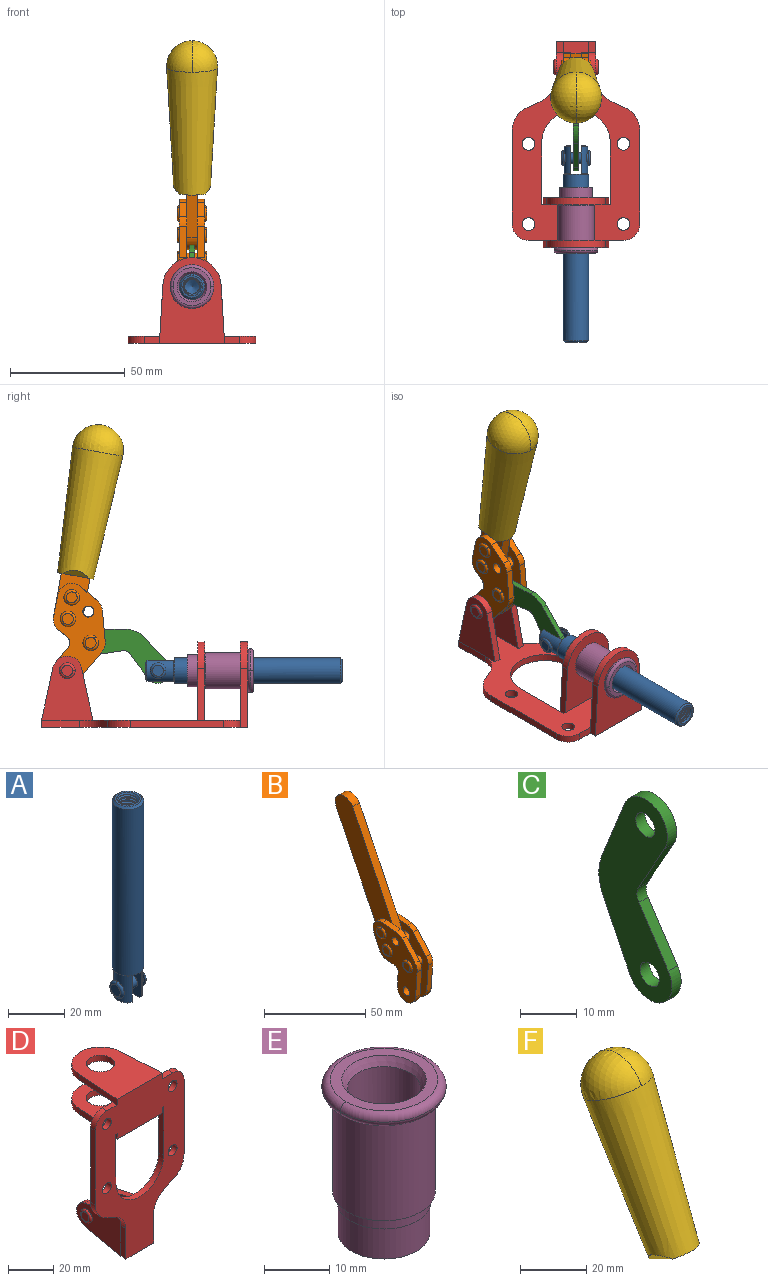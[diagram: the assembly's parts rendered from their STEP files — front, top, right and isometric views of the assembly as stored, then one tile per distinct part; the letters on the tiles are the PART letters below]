
ASSEMBLY  parts=6 mates=6
PART A: 48 faces, bbox 12.6x11.1x86.1 mm
  f0: torus R=2.41mm, axis (-1,0,0), area 15mm2, adj f30,f32,f34
  f1: torus R=2.41mm, axis (-1,0,0), area 15mm2, adj f29,f31,f33
  f2: cylinder r=5.54mm len=72.39mm, axis (0,0,1), area 2518.5mm2, adj f3,f4,f42,f43
  f3: cone r=5.54mm half-angle=45deg, axis (0,0,1), area 7.6mm2, adj f2,f5,f41
  f4: cone r=5.54mm half-angle=45deg, axis (0,0,-1), area 34.9mm2, adj f2,f39
  f5: cylinder r=5.08mm len=11.48mm, axis (0,0,1), area 108.3mm2, adj f3,f7,f8,f41
  f6: cylinder r=2.41mm len=4.83mm, axis (-1,0,0), area 71.2mm2, adj f40,f41
  f7: cylinder r=2.41mm len=4.83mm, axis (-1,0,0), area 7.6mm2, adj f5,f34
  f8: cone r=5.08mm half-angle=45deg, axis (0,0,1), area 10.6mm2, adj f5,f37,f41
  f9: cone r=3.98mm half-angle=45deg, axis (0,0,1), area 17.6mm2, adj f27,f39,f45,f46,f47
  f10: cylinder r=2.41mm len=4.83mm, axis (-1,0,0), area 7.6mm2, adj f33,f38
  f11: cylinder r=3.2mm len=6.4mm, axis (0,0,1), area 78.4mm2, adj f12,f28,f44,f45,f47
  f12: cylinder r=3.2mm len=6.4mm, axis (0,0,1), area 10.5mm2, adj f11,f13,f45,f47
  f13: cylinder r=3.2mm len=6.4mm, axis (0,0,1), area 10.5mm2, adj f12,f14,f45,f47
  f14: cylinder r=3.2mm len=6.4mm, axis (0,0,1), area 10.5mm2, adj f13,f15,f45,f47
  f15: cylinder r=3.2mm len=6.4mm, axis (0,0,1), area 10.5mm2, adj f14,f16,f45,f47
  f16: cylinder r=3.2mm len=6.4mm, axis (0,0,1), area 10.5mm2, adj f15,f17,f45,f47
  f17: cylinder r=3.2mm len=6.4mm, axis (0,0,1), area 10.5mm2, adj f16,f18,f45,f47
  f18: cylinder r=3.2mm len=6.4mm, axis (0,0,1), area 10.5mm2, adj f17,f19,f45,f47
  f19: cylinder r=3.2mm len=6.4mm, axis (0,0,1), area 10.5mm2, adj f18,f20,f45,f47
  f20: cylinder r=3.2mm len=6.4mm, axis (0,0,1), area 10.5mm2, adj f19,f21,f45,f47
  f21: cylinder r=3.2mm len=6.4mm, axis (0,0,1), area 10.5mm2, adj f20,f22,f45,f47
  f22: cylinder r=3.2mm len=6.4mm, axis (0,0,1), area 10.5mm2, adj f21,f23,f45,f47
  f23: cylinder r=3.2mm len=6.4mm, axis (0,0,1), area 10.5mm2, adj f22,f24,f45,f47
  f24: cylinder r=3.2mm len=6.4mm, axis (0,0,1), area 10.5mm2, adj f23,f25,f45,f47
  f25: cylinder r=3.2mm len=6.4mm, axis (0,0,1), area 10.5mm2, adj f24,f26,f45,f47
  f26: cylinder r=3.2mm len=6.4mm, axis (0,0,1), area 10.5mm2, adj f25,f27,f45,f47
  f27: cylinder r=3.2mm len=6.4mm, axis (0,0,1), area 7.4mm2, adj f9,f26,f45,f47
  f28: cone r=3.2mm half-angle=60deg, axis (0,0,1), area 37.2mm2, adj f11
  f29: plane 4.83x4.83mm, normal (-1,0,0), area 18.3mm2, adj f1,f31
  f30: plane 4.83x4.83mm, normal (1,0,0), area 18.3mm2, adj f0,f32
  f31: torus R=2.41mm, axis (-1,0,0), area 15mm2, adj f1,f29,f33
  f32: torus R=2.41mm, axis (-1,0,0), area 15mm2, adj f0,f30,f34
  f33: plane 6.83x6.83mm, normal (1,0,0), area 18.3mm2, adj f1,f10,f31
  f34: plane 6.83x6.83mm, normal (-1,0,0), area 18.3mm2, adj f0,f7,f32
  f35: cone r=5.08mm half-angle=45deg, axis (0,0,1), area 10.6mm2, adj f36,f38,f40
  f36: plane 7.25x1.97mm, normal (0,0,-1), area 10mm2, adj f35,f40
  f37: plane 7.25x1.97mm, normal (0,0,-1), area 10mm2, adj f8,f41
  f38: cylinder r=5.08mm len=11.48mm, axis (0,0,1), area 108.3mm2, adj f10,f35,f40,f42
  f39: plane 9.55x9.55mm, normal (0,0,1), area 22mm2, adj f4,f9
  f40: plane 12.76x10.09mm, normal (1,0,0), area 95.7mm2, adj f6,f35,f36,f38,f42,f43
  f41: plane 12.76x10.09mm, normal (-1,0,0), area 95.7mm2, adj f3,f5,f6,f8,f37,f43
  f42: cone r=5.54mm half-angle=45deg, axis (0,0,1), area 7.6mm2, adj f2,f38,f40
  f43: plane 11.07x4.7mm, normal (0,0,-1), area 50.4mm2, adj f2,f40,f41
  f44: plane 0.89x0.62mm, normal (-1,0,0), area 0.3mm2, adj f11,f45,f46,f47
  f45: bspline ~24.8x7.63mm, area 266.6mm2, adj f9,f11,f12,f13,f14,f15,f16,f17
  f46: bspline ~24.87x7.63mm, area 73.6mm2, adj f9,f44,f45,f47
  f47: bspline ~24.98x7.63mm, area 272.5mm2, adj f9,f11,f12,f13,f14,f15,f16,f17
PART B: 59 faces, bbox 12.9x60.2x99.6 mm
  f0: torus R=2.39mm, axis (-1,0,0), area 14.9mm2, adj f20,f43,f51
  f1: torus R=2.39mm, axis (-1,0,0), area 14.9mm2, adj f19,f42,f51
  f2: torus R=2.39mm, axis (-1,0,0), area 14.9mm2, adj f18,f35,f51
  f3: torus R=2.39mm, axis (-1,0,0), area 14.9mm2, adj f14,f17,f23
  f4: torus R=2.39mm, axis (-1,0,0), area 14.9mm2, adj f13,f16,f23
  f5: torus R=2.39mm, axis (-1,0,0), area 14.9mm2, adj f12,f15,f23
  f6: cylinder r=2.39mm len=4.78mm, axis (1,0,0), area 46.5mm2, adj f48,f50,f51
  f7: cylinder r=2.39mm len=4.78mm, axis (1,0,0), area 46.5mm2, adj f50,f51
  f8: cylinder r=6.35mm len=12.68mm, axis (1,0,0), area 61.8mm2, adj f38,f39,f50,f51
  f9: cylinder r=2.39mm len=4.78mm, axis (-1,0,0), area 70.5mm2, adj f46,f50
  f10: cylinder r=2.39mm len=4.78mm, axis (-1,0,0), area 46.5mm2, adj f23,f45,f46
  f11: cylinder r=2.39mm len=4.78mm, axis (-1,0,0), area 46.5mm2, adj f23,f46
  f12: plane 4.78x4.78mm, normal (1,0,0), area 17.9mm2, adj f5,f15
  f13: plane 4.78x4.78mm, normal (1,0,0), area 17.9mm2, adj f4,f16
  f14: plane 4.78x4.78mm, normal (1,0,0), area 17.9mm2, adj f3,f17
  f15: torus R=2.39mm, axis (-1,0,0), area 14.9mm2, adj f5,f12,f23
  f16: torus R=2.39mm, axis (-1,0,0), area 14.9mm2, adj f4,f13,f23
  f17: torus R=2.39mm, axis (-1,0,0), area 14.9mm2, adj f3,f14,f23
  f18: plane 4.78x4.78mm, normal (-1,0,0), area 17.9mm2, adj f2,f35
  f19: plane 4.78x4.78mm, normal (-1,0,0), area 17.9mm2, adj f1,f42
  f20: plane 4.78x4.78mm, normal (-1,0,0), area 17.9mm2, adj f0,f43
  f21: plane 2.26x0.2mm, normal (1,0,0), area 0.2mm2, adj f31,f44
  f22: plane 2.26x0.2mm, normal (-1,0,0), area 0.2mm2, adj f41,f44
  f23: plane 39.37x30.77mm, normal (1,0,0), area 565.5mm2, adj f3,f4,f5,f10,f11,f15,f16,f17
  f24: cylinder r=6.1mm len=4.15mm, axis (-1,0,0), area 14.7mm2, adj f23,f25,f32,f46
  f25: plane 10.25x9.01mm, normal (0,-0.75,0.66), area 42.3mm2, adj f23,f24,f26,f46
  f26: cylinder r=6.35mm len=4.64mm, axis (-1,0,0), area 15.6mm2, adj f23,f25,f27,f46
  f27: plane 15.84x3.1mm, normal (0,-1,-0.07), area 49.2mm2, adj f23,f26,f28,f46
  f28: cylinder r=6.35mm len=12.68mm, axis (-1,0,0), area 61.8mm2, adj f23,f27,f29,f46
  f29: plane 8.11x3.1mm, normal (0,1,0.07), area 25.2mm2, adj f23,f28,f30,f46
  f30: cylinder r=3.05mm len=3.25mm, axis (-1,0,0), area 14.8mm2, adj f23,f29,f31,f46
  f31: plane 5.99x3.1mm, normal (0,0.07,-1), area 18.6mm2, adj f21,f23,f30,f44,f46
  f32: plane 9.5x3.1mm, normal (0,-0.07,1), area 29.5mm2, adj f23,f24,f33,f46,f47
  f33: cylinder r=6.1mm len=8.63mm, axis (-1,0,0), area 39.1mm2, adj f23,f32,f34,f47
  f34: plane 8.65x3.96mm, normal (0,0.91,-0.42), area 29.5mm2, adj f23,f33,f44,f47
  f35: torus R=2.39mm, axis (-1,0,0), area 14.9mm2, adj f2,f18,f51
  f36: plane 10.25x9.01mm, normal (0,-0.75,0.66), area 42.3mm2, adj f37,f49,f50,f51
  f37: cylinder r=6.35mm len=4.64mm, axis (1,0,0), area 15.6mm2, adj f36,f38,f50,f51
  f38: plane 15.84x3.1mm, normal (0,-1,-0.07), area 49.2mm2, adj f8,f37,f50,f51
  f39: plane 8.11x3.1mm, normal (0,1,0.07), area 25.2mm2, adj f8,f40,f50,f51
  f40: cylinder r=3.05mm len=3.25mm, axis (1,0,0), area 14.8mm2, adj f39,f41,f50,f51
  f41: plane 5.99x3.1mm, normal (0,0.07,-1), area 18.6mm2, adj f22,f40,f44,f50,f51
  f42: torus R=2.39mm, axis (-1,0,0), area 14.9mm2, adj f1,f19,f51
  f43: torus R=2.39mm, axis (-1,0,0), area 14.9mm2, adj f0,f20,f51
  f44: cylinder r=6.35mm len=12.12mm, axis (-1,0,0), area 128.9mm2, adj f21,f22,f23,f31,f34,f41,f46,f47
  f45: plane 2.65x1.35mm, normal (1,0,0), area 1mm2, adj f10,f55
  f46: plane 39.08x20.42mm, normal (-1,0,0), area 412.5mm2, adj f9,f10,f11,f24,f25,f26,f27,f28
  f47: plane 77.62x39.82mm, normal (1,0,0), area 850mm2, adj f32,f33,f34,f44,f53,f54,f55
  f48: plane 2.65x1.35mm, normal (-1,0,0), area 1mm2, adj f6,f55
  f49: cylinder r=6.1mm len=4.15mm, axis (1,0,0), area 14.7mm2, adj f36,f50,f51,f56
  f50: plane 39.08x20.42mm, normal (1,0,0), area 412.5mm2, adj f6,f7,f8,f9,f36,f37,f38,f39
  f51: plane 39.37x30.77mm, normal (-1,0,0), area 565.5mm2, adj f0,f1,f2,f6,f7,f8,f35,f36
  f52: plane 8.65x3.96mm, normal (0,0.91,-0.42), area 29.5mm2, adj f44,f51,f57,f58
  f53: plane 68.49x33.4mm, normal (0,0.9,-0.44), area 358.1mm2, adj f44,f47,f54,f58
  f54: cylinder r=6.35mm len=12.06mm, axis (1,0,0), area 93.7mm2, adj f47,f53,f55,f58
  f55: plane 68.49x33.4mm, normal (0,-0.9,0.44), area 358.1mm2, adj f44,f45,f46,f47,f48,f50,f54,f58
  f56: plane 9.5x3.1mm, normal (0,-0.07,1), area 29.5mm2, adj f49,f50,f51,f57,f58
  f57: cylinder r=6.1mm len=8.63mm, axis (1,0,0), area 39.1mm2, adj f51,f52,f56,f58
  f58: plane 77.62x39.82mm, normal (-1,0,0), area 850mm2, adj f44,f52,f53,f54,f55,f56,f57
PART C: 12 faces, bbox 2.3x18.2x42.8 mm
  f0: cylinder r=2.4mm len=4.8mm, axis (1,0,0), area 34.9mm2, adj f4,f11
  f1: cylinder r=10.41mm len=8.47mm, axis (1,0,0), area 20.2mm2, adj f4,f9,f10,f11
  f2: cylinder r=3.05mm len=3.16mm, axis (1,0,0), area 7.7mm2, adj f4,f6,f7,f11
  f3: cylinder r=2.4mm len=4.8mm, axis (1,0,0), area 34.9mm2, adj f4,f11
  f4: plane 42.81x18.23mm, normal (-1,0,0), area 414.1mm2, adj f0,f1,f2,f3,f5,f6,f7,f8
  f5: cylinder r=5.54mm len=10.67mm, axis (1,0,0), area 41.8mm2, adj f4,f6,f10,f11
  f6: plane 11.66x6.53mm, normal (0,-0.87,-0.49), area 30.9mm2, adj f2,f4,f5,f11
  f7: plane 11.17x7.33mm, normal (0,-0.84,0.55), area 30.9mm2, adj f2,f4,f8,f11
  f8: cylinder r=5.54mm len=10.51mm, axis (1,0,0), area 41.8mm2, adj f4,f7,f9,f11
  f9: plane 13.67x6.67mm, normal (0,0.9,-0.44), area 35.1mm2, adj f1,f4,f8,f11
  f10: plane 14.1x5.7mm, normal (0,0.93,0.37), area 35.1mm2, adj f1,f4,f5,f11
  f11: plane 42.81x18.23mm, normal (1,0,0), area 414.1mm2, adj f0,f1,f2,f3,f5,f6,f7,f8
PART D: 55 faces, bbox 55.7x37.4x89.8 mm
  f0: torus R=2.41mm, axis (-1,0,0), area 15mm2, adj f11,f15,f25
  f1: torus R=2.41mm, axis (-1,0,0), area 15mm2, adj f10,f12,f22
  f2: cylinder r=2.78mm len=5.56mm, axis (0,-1,0), area 54.2mm2, adj f30,f54
  f3: cylinder r=14.99mm len=29.97mm, axis (0,-1,0), area 145.9mm2, adj f30,f49,f53,f54
  f4: cylinder r=2.78mm len=5.56mm, axis (0,-1,0), area 54.2mm2, adj f30,f54
  f5: cylinder r=2.78mm len=5.56mm, axis (0,-1,0), area 54.2mm2, adj f30,f54
  f6: cylinder r=2.78mm len=5.56mm, axis (0,-1,0), area 54.2mm2, adj f30,f54
  f7: cylinder r=6.35mm len=12.7mm, axis (0,0,1), area 123.6mm2, adj f27,f51
  f8: cylinder r=6.35mm len=12.7mm, axis (0,0,-1), area 124.7mm2, adj f21,f35
  f9: cylinder r=2.41mm len=11.18mm, axis (-1,0,0), area 169.4mm2, adj f16,f19
  f10: plane 4.83x4.83mm, normal (1,0,0), area 18.3mm2, adj f1,f12
  f11: plane 4.83x4.83mm, normal (-1,0,0), area 18.3mm2, adj f0,f15
  f12: torus R=2.41mm, axis (-1,0,0), area 15mm2, adj f1,f10,f22
  f13: cylinder r=6.35mm len=12.41mm, axis (1,0,0), area 53.4mm2, adj f18,f19,f22,f23
  f14: cylinder r=6.35mm len=12.41mm, axis (-1,0,0), area 53.4mm2, adj f16,f17,f24,f25
  f15: torus R=2.41mm, axis (-1,0,0), area 15mm2, adj f0,f11,f25
  f16: plane 27.86x22.35mm, normal (1,0,0), area 425.4mm2, adj f9,f14,f17,f24,f30
  f17: plane 22.86x4.97mm, normal (0,0.21,0.98), area 72.5mm2, adj f14,f16,f25,f30
  f18: plane 22.86x4.97mm, normal (0,0.21,0.98), area 72.5mm2, adj f13,f19,f22,f30
  f19: plane 27.86x22.35mm, normal (-1,0,0), area 425.4mm2, adj f9,f13,f18,f23,f30
  f20: cylinder r=12.7mm len=25.35mm, axis (0,0,-1), area 119.8mm2, adj f21,f34,f35,f36
  f21: plane 34.21x28.07mm, normal (0,0,-1), area 702.4mm2, adj f8,f20,f30,f34,f36
  f22: plane 27.96x22.45mm, normal (1,0,0), area 407.2mm2, adj f1,f12,f13,f18,f23,f30,f42,f43
  f23: plane 22.86x4.97mm, normal (0,0.21,-0.98), area 72.5mm2, adj f13,f19,f22,f44
  f24: plane 22.86x4.97mm, normal (0,0.21,-0.98), area 72.5mm2, adj f14,f16,f25,f44
  f25: plane 27.86x22.35mm, normal (-1,0,0), area 407.1mm2, adj f0,f14,f15,f17,f24,f30,f45,f46
  f26: plane 3.1x0.95mm, normal (0,0,-1), area 2.7mm2, adj f30,f49,f50,f54
  f27: plane 34.21x28.07mm, normal (0,0,1), area 702.4mm2, adj f7,f28,f30,f50,f52
  f28: cylinder r=12.7mm len=25.35mm, axis (0,0,1), area 118.8mm2, adj f27,f50,f51,f52
  f29: plane 3.1x0.95mm, normal (0,0,-1), area 2.7mm2, adj f30,f52,f53,f54
  f30: plane 86.54x55.63mm, normal (0,1,0), area 2362.9mm2, adj f2,f3,f4,f5,f6,f16,f17,f18
  f31: plane 40.56x3.1mm, normal (-1,0,0), area 125.7mm2, adj f30,f32,f48,f54
  f32: cylinder r=7.11mm len=7.11mm, axis (0,-1,0), area 34.6mm2, adj f30,f31,f33,f54
  f33: plane 6.67x3.1mm, normal (0,0,1), area 20.4mm2, adj f30,f32,f34,f54
  f34: plane 25.39x3.13mm, normal (-1,0.06,0), area 79.5mm2, adj f20,f21,f33,f35,f54
  f35: plane 37.31x28.45mm, normal (0,0,1), area 789.9mm2, adj f8,f20,f34,f36,f54
  f36: plane 25.39x3.13mm, normal (1,0.06,0), area 79.5mm2, adj f20,f21,f35,f37,f54
  f37: plane 6.67x3.1mm, normal (0,0,1), area 20.4mm2, adj f30,f36,f38,f54
  f38: cylinder r=7.11mm len=7.11mm, axis (0,-1,0), area 34.6mm2, adj f30,f37,f39,f54
  f39: plane 40.56x3.1mm, normal (1,0,0), area 125.7mm2, adj f30,f38,f40,f54
  f40: cylinder r=11.18mm len=10.16mm, axis (0,-1,0), area 39.5mm2, adj f30,f39,f41,f54
  f41: plane 6.09x3.1mm, normal (0.42,0,-0.91), area 20.8mm2, adj f30,f40,f42,f54
  f42: cylinder r=11.18mm len=9.41mm, axis (0,-1,0), area 37.2mm2, adj f22,f30,f41,f43,f54
  f43: plane 16.5x3.1mm, normal (1,0,0), area 51.1mm2, adj f22,f42,f44,f54
  f44: plane 17.37x3.1mm, normal (0,0,-1), area 53.8mm2, adj f23,f24,f30,f43,f45,f54
  f45: plane 16.5x3.1mm, normal (-1,0,0), area 51.1mm2, adj f25,f44,f46,f54
  f46: cylinder r=11.18mm len=9.41mm, axis (0,-1,0), area 37.2mm2, adj f25,f30,f45,f47,f54
  f47: plane 6.09x3.1mm, normal (-0.42,0,-0.91), area 20.8mm2, adj f30,f46,f48,f54
  f48: cylinder r=11.18mm len=10.16mm, axis (0,-1,0), area 39.5mm2, adj f30,f31,f47,f54
  f49: plane 26.54x3.1mm, normal (-1,0,0), area 82.3mm2, adj f3,f26,f30,f54
  f50: plane 25.39x3.1mm, normal (1,0.06,0), area 78.8mm2, adj f26,f27,f28,f51,f54
  f51: plane 37.31x28.45mm, normal (0,0,-1), area 789.9mm2, adj f7,f28,f50,f52,f54
  f52: plane 25.39x3.1mm, normal (-1,0.06,0), area 78.8mm2, adj f27,f28,f29,f51,f54
  f53: plane 26.54x3.1mm, normal (1,0,0), area 82.3mm2, adj f3,f29,f30,f54
  f54: plane 89.66x55.63mm, normal (0,-1,0), area 2678.5mm2, adj f2,f3,f4,f5,f6,f26,f29,f31
PART E: 15 faces, bbox 20.6x20.6x28.7 mm
  f0: torus R=8.26mm, axis (0,0,1), area 56.8mm2, adj f1,f10,f12
  f1: torus R=8.26mm, axis (0,0,1), area 56.8mm2, adj f0,f6,f13
  f2: cylinder r=5.59mm len=25.91mm, axis (0,0,1), area 909.6mm2, adj f3,f4
  f3: cone r=6.86mm half-angle=45deg, axis (0,0,-1), area 70.2mm2, adj f2,f14
  f4: cone r=6.47mm half-angle=30deg, axis (0,0,1), area 66.7mm2, adj f2,f13
  f5: cylinder r=7.04mm len=14.07mm, axis (0,0,1), area 252.6mm2, adj f11,f14
  f6: torus R=8.26mm, axis (0,0,1), area 56.8mm2, adj f1,f12,f13
  f7: cylinder r=7.16mm len=14.33mm, axis (0,0,1), area 91.5mm2, adj f9,f11
  f8: cylinder r=7.86mm len=18.42mm, axis (0,0,1), area 909.6mm2, adj f9,f10
  f9: plane 15.72x15.72mm, normal (0,0,-1), area 33mm2, adj f7,f8
  f10: plane 16.51x16.51mm, normal (0,0,-1), area 19.9mm2, adj f0,f8,f12
  f11: plane 14.33x14.33mm, normal (0,0,-1), area 5.7mm2, adj f5,f7
  f12: torus R=8.26mm, axis (0,0,1), area 56.8mm2, adj f0,f6,f10
  f13: plane 16.51x16.51mm, normal (0,0,1), area 82.7mm2, adj f1,f4,f6
  f14: plane 14.07x14.07mm, normal (0,0,-1), area 7.8mm2, adj f3,f5
PART F: 11 faces, bbox 22.3x42.6x64.5 mm
  f0: sphere r=11.13mm, area 411.4mm2, adj f1,f8
  f1: cone r=11.11mm half-angle=3.3deg, axis (0,0.44,0.9), area 3251.8mm2, adj f0,f7,f8,f9,f10
  f2: cylinder r=6.16mm len=11.7mm, axis (1,0,0), area 89.5mm2, adj f3,f4,f5,f6
  f3: plane 60.23x36.75mm, normal (-1,0,0), area 763.6mm2, adj f2,f4,f6,f10
  f4: plane 51.37x25.05mm, normal (0,0.9,-0.44), area 264.2mm2, adj f2,f3,f5,f10
  f5: plane 60.23x36.75mm, normal (1,0,0), area 763.6mm2, adj f2,f4,f6,f10
  f6: plane 51.37x25.05mm, normal (0,-0.9,0.44), area 264.2mm2, adj f2,f3,f5,f10
  f7: plane 9.95x5.95mm, normal (0.71,-0.31,-0.64), area 25.8mm2, adj f1,f10
  f8: sphere r=11.13mm, area 411.4mm2, adj f0,f1
  f9: plane 9.95x5.95mm, normal (-0.71,-0.31,-0.64), area 25.8mm2, adj f1,f10
  f10: plane 14.27x11.38mm, normal (0,-0.44,-0.9), area 106.7mm2, adj f1,f3,f4,f5,f6,f7,f9
PLACE A rot(axis=(1,0,0),90deg) t=(0,17.44,0)mm
PLACE B rot(axis=(1,0,0),36.1deg) t=(0,2.73,36.05)mm
PLACE C rot(axis=(1,0,0),114.5deg) t=(0,26.25,8.63)mm
PLACE D rot(axis=(1,0,0),90deg) t=(0,9.43,0)mm fixed
PLACE E rot(axis=(1,0,0),90deg) t=(0,9.43,0)mm
PLACE F rot(axis=(1,0,0),36.1deg) t=(0.04,2.73,36.05)mm
MATE fastened E.f2 <-> D.f7  axis (0,1,0) through (0,-36.96,24.61)mm
MATE slider A.f2 <-> D.f7  axis (0,-1,0) through (0,-41.34,24.61)mm
MATE revolute B.f7 <-> D.f0  axis (-1,0,0) through (0,41.52,24.61)mm
MATE revolute C.f5 <-> A.f6  axis (1,0,0) through (0,1.96,24.61)mm
MATE fastened F.f2 <-> B.f54  axis (-1,0,0) through (2.35,27.88,122.16)mm
MATE revolute C.f3 <-> B.f4  axis (1,0,0) through (0,31.3,36.76)mm
